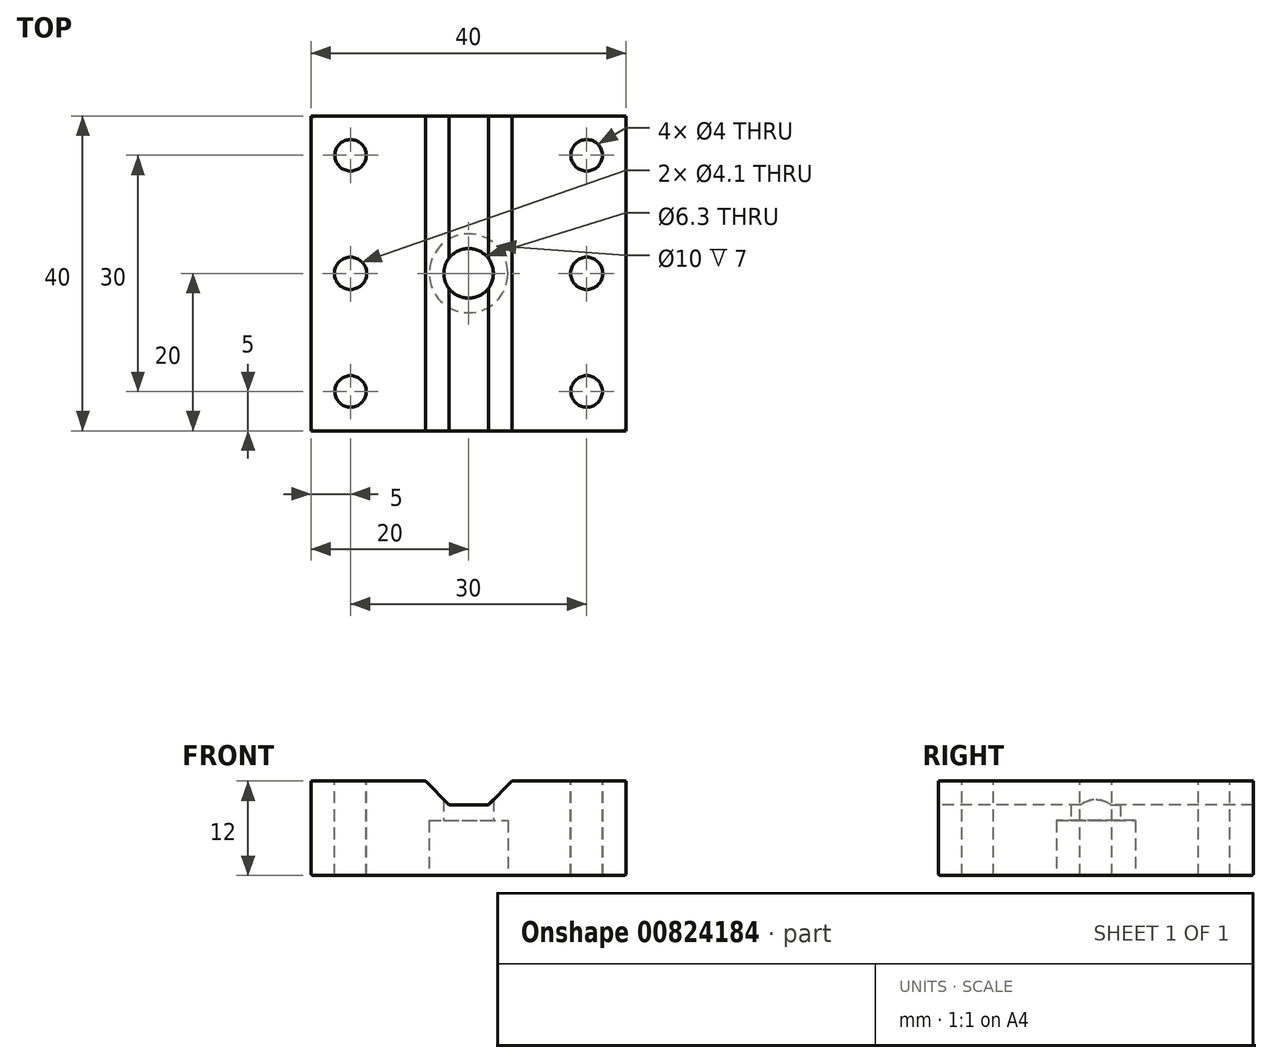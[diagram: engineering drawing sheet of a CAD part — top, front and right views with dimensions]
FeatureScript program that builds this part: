
annotation { "Feature Type Name" : "Feature", "Feature Type Description" : "" }
export const myFeature = defineFeature(function(context is Context, id is Id, definition is map)
    precondition{}
    {
        {
            var Q0;
            Q0=qCreatedBy(makeId("Top.planeOp"),FACE);
            var sketch = newSketch(context, id + "F0", { "sketchPlane" : qUnion([Q0])});
            skLineSegment(sketch, "E0.bottom", {"start": v(0, 0) * mm, "end": v(40, 0) * mm});
            skLineSegment(sketch, "E0.top", {"start": v(0, 40) * mm, "end": v(40, 40) * mm});
            skLineSegment(sketch, "E0.left", {"start": v(0, 0) * mm, "end": v(0, 40) * mm});
            skLineSegment(sketch, "E0.right", {"start": v(40, 0) * mm, "end": v(40, 40) * mm});
            skSolve(sketch);
        }
        {
            var Q0;
            Q0 = qSketchRegion(id + "F0", true);
            extrude(context, id + "F1", {"entities" : qUnion([Q0]), "depth" : 12 * mm, "offsetDistance" : 25 * mm});
        }
        {
            var Q0;
            Q0=makeQuery(id+"F1.opExtrude","SWEPT_FACE",FACE,{"disambiguationData":[OSD([sQuery(id+"F0.wireOp",EDGE,"E0.bottom")])]});
            var sketch = newSketch(context, id + "F2", { "sketchPlane" : qUnion([Q0])});
            skLineSegment(sketch, "E1.top", {"start": v(17.5, 9) * mm, "end": v(22.5, 9) * mm});
            skLineSegment(sketch, "E2", {"start": v(22.5, 9) * mm, "end": v(25.5, 12) * mm});
            skLineSegment(sketch, "E3", {"start": v(14.5, 12) * mm, "end": v(17.5, 9) * mm});
            skLineSegment(sketch, "E4", {"start": v(14.5, 12) * mm, "end": v(25.5, 12) * mm});
            skLineSegment(sketch, "E5", {"start": v(0, 12) * mm, "end": v(14.5, 12) * mm, "construction": true});
            skLineSegment(sketch, "E6", {"start": v(25.5, 12) * mm, "end": v(40, 12) * mm, "construction": true});
            skSolve(sketch);
        }
        {
            var Q0;
            Q0 = qSketchRegion(id + "F2", true);
            extrude(context, id + "F3", {"entities" : qUnion([Q0]), "operationType" : NewBodyOperationType.REMOVE, "endBound" : BoundingType.THROUGH_ALL, "oppositeDirection" : true, "depth" : 25 * mm, "offsetDistance" : 25 * mm});
        }
        {
            var Q0;
            {var subQ0=sQuery(id+"F0.wireOp",EDGE,"E0.bottom");var subQ1=sQuery(id+"F0.wireOp",EDGE,"E0.top");var subQ2=sQuery(id+"F0.wireOp",EDGE,"E0.left");Q0=makeQuery(id+"F3.boolean.opBoolean","SPLIT",FACE,{"disambiguationData":[TD([makeQuery(id+"F1.opExtrude","SWEPT_FACE",FACE,{"disambiguationData":[OSD([subQ2])]})])],"derivedFrom":makeQuery(id+"F1.opExtrude","CAP_FACE",FACE,{"disambiguationData":[OSD([subQ0,subQ1,subQ2,sQuery(id+"F0.wireOp",EDGE,"E0.right")])],"isStart":false})});}
            var sketch = newSketch(context, id + "F4", { "sketchPlane" : qUnion([Q0])});
            skLineSegment(sketch, "E7", {"start": v(5, 40) * mm, "end": v(5, 0) * mm, "construction": true});
            skPoint(sketch, "E7.endSnap0", {"position": v(7.25, 0) * mm});
            skCircle(sketch, "E8", {"center": v(5, 5) * mm, "radius": 2 * mm});
            skCircle(sketch, "E9.0.1.0", {"center": v(5, 35) * mm, "radius": 2 * mm});
            skCircle(sketch, "E9.1.0.0", {"center": v(35, 5) * mm, "radius": 2 * mm});
            skCircle(sketch, "E9.1.1.0", {"center": v(35, 35) * mm, "radius": 2 * mm});
            skLineSegment(sketch, "E9.direction1", {"start": v(5, 5) * mm, "end": v(35, 5) * mm, "construction": true});
            skLineSegment(sketch, "E9.direction2", {"start": v(5, 5) * mm, "end": v(5, 35) * mm, "construction": true});
            skSolve(sketch);
        }
        {
            var Q0;
            Q0 = qSketchRegion(id + "F4", true);
            extrude(context, id + "F5", {"entities" : qUnion([Q0]), "operationType" : NewBodyOperationType.REMOVE, "endBound" : BoundingType.THROUGH_ALL, "oppositeDirection" : true, "depth" : 25 * mm, "offsetDistance" : 25 * mm});
        }
        {
            var Q0;
            {var subQ0=sQuery(id+"F0.wireOp",EDGE,"E0.bottom");var subQ1=sQuery(id+"F0.wireOp",EDGE,"E0.top");var subQ2=sQuery(id+"F0.wireOp",EDGE,"E0.left");Q0=makeQuery(id+"F3.boolean.opBoolean","SPLIT",FACE,{"disambiguationData":[TD([makeQuery(id+"F1.opExtrude","SWEPT_FACE",FACE,{"disambiguationData":[OSD([subQ2])]})])],"derivedFrom":makeQuery(id+"F1.opExtrude","CAP_FACE",FACE,{"disambiguationData":[OSD([subQ0,subQ1,subQ2,sQuery(id+"F0.wireOp",EDGE,"E0.right")])],"isStart":false})});}
            var sketch = newSketch(context, id + "F6", { "sketchPlane" : qUnion([Q0])});
            skLineSegment(sketch, "E10", {"start": v(0, 20) * mm, "end": v(47.25, 20) * mm, "construction": true});
            skCircle(sketch, "E11", {"center": v(5, 20) * mm, "radius": 2.05 * mm});
            skCircle(sketch, "E12", {"center": v(35, 20) * mm, "radius": 2.05 * mm});
            skSolve(sketch);
        }
        {
            var Q0;
            Q0 = qSketchRegion(id + "F6", true);
            extrude(context, id + "F7", {"entities" : qUnion([Q0]), "operationType" : NewBodyOperationType.REMOVE, "endBound" : BoundingType.THROUGH_ALL, "oppositeDirection" : true, "depth" : 25 * mm, "offsetDistance" : 25 * mm});
        }
        {
            var Q0;
            Q0=makeQuery(id+"F1.opExtrude","CAP_EDGE",EDGE,{"disambiguationData":[OSD([sQuery(id+"F0.wireOp",EDGE,"E0.bottom")])],"isStart":true});
            var Q1;
            Q1=makeQuery(id+"F1.opExtrude","CAP_EDGE",EDGE,{"disambiguationData":[OSD([sQuery(id+"F0.wireOp",EDGE,"E0.left")])],"isStart":true});
            var Q2;
            Q2=makeQuery(id+"F1.opExtrude","CAP_EDGE",EDGE,{"disambiguationData":[OSD([sQuery(id+"F0.wireOp",EDGE,"E0.right")])],"isStart":true});
            var Q3;
            Q3=makeQuery(id+"F1.opExtrude","CAP_EDGE",EDGE,{"disambiguationData":[OSD([sQuery(id+"F0.wireOp",EDGE,"E0.top")])],"isStart":true});
            fillet(context, id + "F8", {"entities" : qUnion([Q0, Q1, Q2, Q3]), "radius" : 0.25 * mm, "tangentPropagation" : true, "allowEdgeOverflow" : false});
        }
        {
            var Q0;
            Q0=makeQuery(id+"F1.opExtrude","CAP_FACE",FACE,{"disambiguationData":[OSD([sQuery(id+"F0.wireOp",EDGE,"E0.bottom"),sQuery(id+"F0.wireOp",EDGE,"E0.top"),sQuery(id+"F0.wireOp",EDGE,"E0.left"),sQuery(id+"F0.wireOp",EDGE,"E0.right")])],"isStart":true});
            var sketch = newSketch(context, id + "F9", { "sketchPlane" : qUnion([Q0])});
            skLineSegment(sketch, "E13", {"start": v(20, 0) * mm, "end": v(20, -40) * mm, "construction": true});
            skCircle(sketch, "E14", {"center": v(20, -20) * mm, "radius": 3.15 * mm});
            skSolve(sketch);
        }
        {
            var Q0;
            Q0 = qSketchRegion(id + "F9", true);
            extrude(context, id + "F10", {"entities" : qUnion([Q0]), "operationType" : NewBodyOperationType.REMOVE, "endBound" : BoundingType.THROUGH_ALL, "oppositeDirection" : true, "depth" : 25 * mm, "offsetDistance" : 25 * mm});
        }
        {
            var Q0;
            Q0=makeQuery(id+"F1.opExtrude","CAP_FACE",FACE,{"disambiguationData":[OSD([sQuery(id+"F0.wireOp",EDGE,"E0.bottom"),sQuery(id+"F0.wireOp",EDGE,"E0.top"),sQuery(id+"F0.wireOp",EDGE,"E0.left"),sQuery(id+"F0.wireOp",EDGE,"E0.right")])],"isStart":true});
            var sketch = newSketch(context, id + "F11", { "sketchPlane" : qUnion([Q0])});
            skCircle(sketch, "E15", {"center": v(20, -20) * mm, "radius": 5 * mm});
            skSolve(sketch);
        }
        {
            var Q0;
            Q0 = qSketchRegion(id + "F11", true);
            extrude(context, id + "F12", {"entities" : qUnion([Q0]), "operationType" : NewBodyOperationType.REMOVE, "oppositeDirection" : true, "depth" : 7 * mm, "offsetDistance" : 25 * mm});
        }
    });
